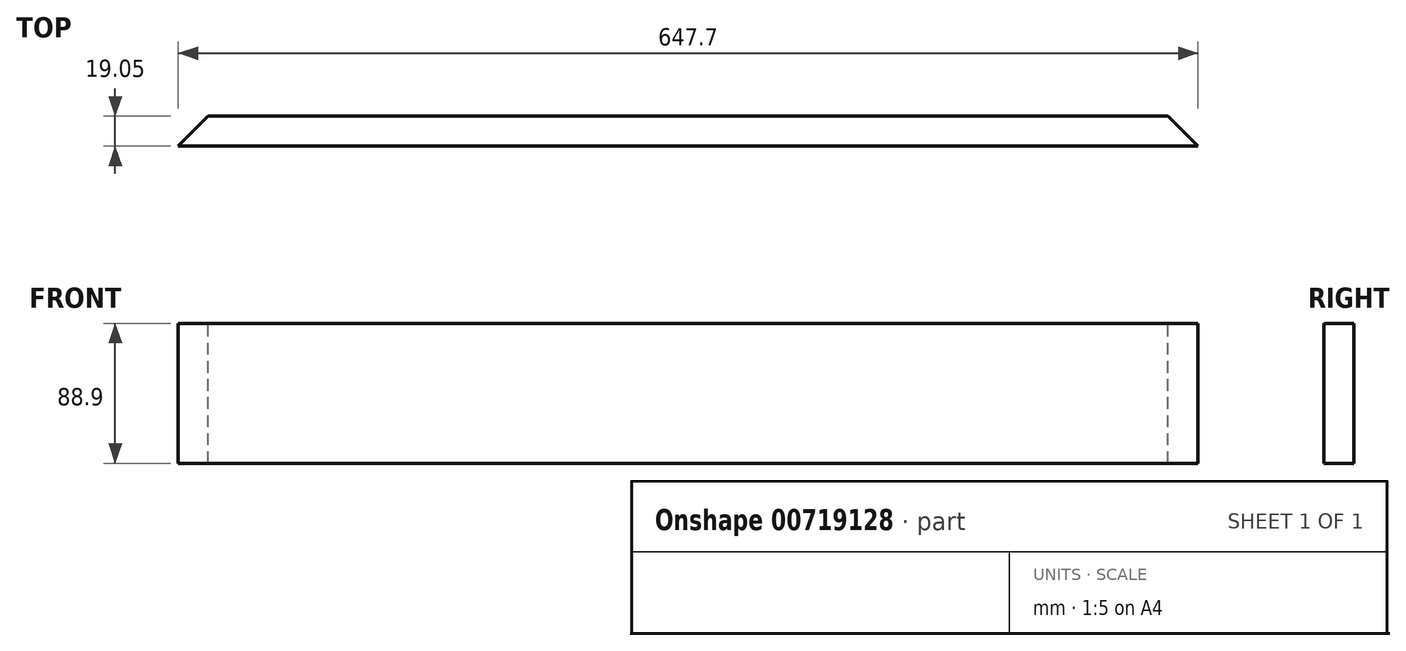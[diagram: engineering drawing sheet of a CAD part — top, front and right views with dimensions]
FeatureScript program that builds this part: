
annotation { "Feature Type Name" : "Feature", "Feature Type Description" : "" }
export const myFeature = defineFeature(function(context is Context, id is Id, definition is map)
    precondition{}
    {
        {
            var Q0;
            Q0=qCreatedBy(makeId("Front.planeOp"),FACE);
            var sketch = newSketch(context, id + "F0", { "sketchPlane" : qUnion([Q0])});
            skLineSegment(sketch, "E0.bottom", {"start": v(0, 0) * mm, "end": v(-647.7, 0) * mm});
            skLineSegment(sketch, "E0.top", {"start": v(0, 88.9) * mm, "end": v(-647.7, 88.9) * mm});
            skLineSegment(sketch, "E0.left", {"start": v(0, 0) * mm, "end": v(0, 88.9) * mm});
            skLineSegment(sketch, "E0.right", {"start": v(-647.7, 0) * mm, "end": v(-647.7, 88.9) * mm});
            skSolve(sketch);
        }
        {
            var Q0;
            Q0 = qSketchRegion(id + "F0", true);
            extrude(context, id + "F1", {"entities" : qUnion([Q0]), "depth" : 19.05 * mm, "offsetDistance" : 25.4 * mm});
        }
        {
            var Q0;
            Q0=makeQuery(id+"F1.opExtrude","SWEPT_FACE",FACE,{"disambiguationData":[OSD([sQuery(id+"F0.wireOp",EDGE,"E0.top")])]});
            var sketch = newSketch(context, id + "F2", { "sketchPlane" : qUnion([Q0])});
            skLineSegment(sketch, "E1", {"start": v(-647.7, -19.05) * mm, "end": v(-628.65, 0) * mm});
            skLineSegment(sketch, "E2", {"start": v(-628.65, 0) * mm, "end": v(-647.7, 0) * mm});
            skLineSegment(sketch, "E3", {"start": v(-647.7, 0) * mm, "end": v(-647.7, -19.05) * mm});
            skSolve(sketch);
        }
        {
            var Q0;
            Q0 = qSketchRegion(id + "F2", true);
            extrude(context, id + "F3", {"entities" : qUnion([Q0]), "operationType" : NewBodyOperationType.REMOVE, "oppositeDirection" : true, "depth" : 127 * mm, "offsetDistance" : 25.4 * mm});
        }
        {
            var Q0;
            Q0=makeQuery(id+"F1.opExtrude","SWEPT_FACE",FACE,{"disambiguationData":[OSD([sQuery(id+"F0.wireOp",EDGE,"E0.top")])]});
            var sketch = newSketch(context, id + "F4", { "sketchPlane" : qUnion([Q0])});
            skLineSegment(sketch, "E4", {"start": v(0, -19.05) * mm, "end": v(-19.05, 0) * mm});
            skLineSegment(sketch, "E5", {"start": v(-19.05, 0) * mm, "end": v(0, 0) * mm});
            skLineSegment(sketch, "E6", {"start": v(0, 0) * mm, "end": v(0, -19.05) * mm});
            skSolve(sketch);
        }
        {
            var Q0;
            Q0 = qSketchRegion(id + "F4", true);
            extrude(context, id + "F5", {"entities" : qUnion([Q0]), "operationType" : NewBodyOperationType.REMOVE, "oppositeDirection" : true, "depth" : 127 * mm, "offsetDistance" : 25.4 * mm});
        }
    });
